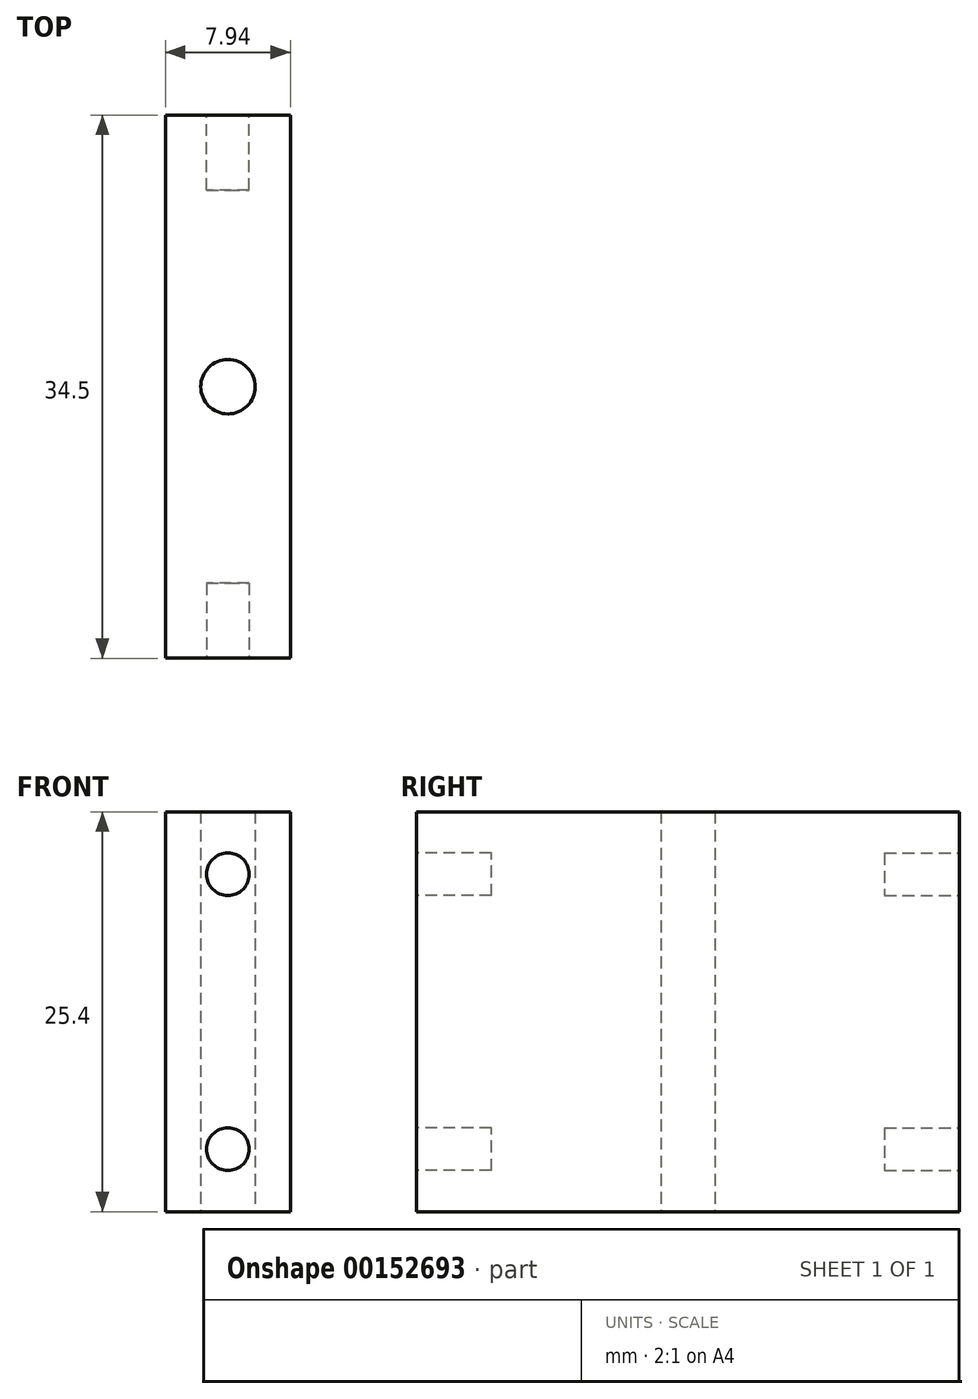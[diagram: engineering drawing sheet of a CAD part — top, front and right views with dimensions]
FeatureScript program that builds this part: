
annotation { "Feature Type Name" : "Feature", "Feature Type Description" : "" }
export const myFeature = defineFeature(function(context is Context, id is Id, definition is map)
    precondition{}
    {
        {
            var Q0;
            Q0=qCreatedBy(makeId("Top.planeOp"),FACE);
            var sketch = newSketch(context, id + "F0", { "sketchPlane" : qUnion([Q0])});
            skLineSegment(sketch, "E0.bottom", {"start": v(3.97, -17.25) * mm, "end": v(-3.97, -17.25) * mm});
            skLineSegment(sketch, "E0.top", {"start": v(3.97, 17.25) * mm, "end": v(-3.97, 17.25) * mm});
            skLineSegment(sketch, "E0.left", {"start": v(3.97, -17.25) * mm, "end": v(3.97, 17.25) * mm});
            skLineSegment(sketch, "E0.right", {"start": v(-3.97, -17.25) * mm, "end": v(-3.97, 17.25) * mm});
            skPoint(sketch, "E0.middle", {"position": v(0, 0) * mm});
            skCircle(sketch, "E1", {"center": v(0, 0) * mm, "radius": 1.73 * mm});
            skSolve(sketch);
        }
        {
            var Q0;
            Q0 = qSketchRegion(id + "F0", true);
            extrude(context, id + "F1", {"entities" : qUnion([Q0]), "depth" : 25.4 * mm});
        }
        {
            var Q0;
            Q0=makeQuery(id+"F1.opExtrude","SWEPT_FACE",FACE,{"disambiguationData":[OSD([sQuery(id+"F0.wireOp",EDGE,"E0.top")])]});
            var sketch = newSketch(context, id + "F2", { "sketchPlane" : qUnion([Q0])});
            skLineSegment(sketch, "E2.bottom", {"start": v(0, 25.4) * mm, "end": v(-3.97, 25.4) * mm, "construction": true});
            skLineSegment(sketch, "E2.top", {"start": v(0, 21.43) * mm, "end": v(-3.97, 21.43) * mm, "construction": true});
            skLineSegment(sketch, "E2.left", {"start": v(0, 25.4) * mm, "end": v(0, 21.43) * mm, "construction": true});
            skLineSegment(sketch, "E2.right", {"start": v(-3.97, 25.4) * mm, "end": v(-3.97, 21.43) * mm, "construction": true});
            skLineSegment(sketch, "E3.bottom", {"start": v(0, 0) * mm, "end": v(-3.97, 0) * mm, "construction": true});
            skLineSegment(sketch, "E3.top", {"start": v(0, 3.97) * mm, "end": v(-3.97, 3.97) * mm, "construction": true});
            skLineSegment(sketch, "E3.left", {"start": v(0, 0) * mm, "end": v(0, 3.97) * mm, "construction": true});
            skLineSegment(sketch, "E3.right", {"start": v(-3.97, 0) * mm, "end": v(-3.97, 3.97) * mm, "construction": true});
            skCircle(sketch, "E4", {"center": v(0, 3.97) * mm, "radius": 1.35 * mm});
            skCircle(sketch, "E5", {"center": v(0, 21.43) * mm, "radius": 1.35 * mm});
            skSolve(sketch);
        }
        {
            var Q0;
            Q0 = qSketchRegion(id + "F2", true);
            extrude(context, id + "F3", {"entities" : qUnion([Q0]), "operationType" : NewBodyOperationType.REMOVE, "oppositeDirection" : true, "depth" : 4.76 * mm});
        }
        {
            var Q0;
            Q0=makeQuery(id+"F1.opExtrude","SWEPT_FACE",FACE,{"disambiguationData":[OSD([sQuery(id+"F0.wireOp",EDGE,"E0.bottom")])]});
            var sketch = newSketch(context, id + "F4", { "sketchPlane" : qUnion([Q0])});
            skCircle(sketch, "E6", {"center": v(0, 21.43) * mm, "radius": 1.35 * mm});
            skCircle(sketch, "E7", {"center": v(0, 3.97) * mm, "radius": 1.35 * mm});
            skSolve(sketch);
        }
        {
            var Q0;
            Q0 = qSketchRegion(id + "F4", true);
            extrude(context, id + "F5", {"entities" : qUnion([Q0]), "operationType" : NewBodyOperationType.REMOVE, "oppositeDirection" : true, "depth" : 4.76 * mm});
        }
    });
